# Revit family: LZSG8WSLK
name_source: partatom
category: Plumbing Fixtures
units: mm (PartAtom-declared; Revit-internal decimal feet)

## family parameters
Cut with Voids When Loaded = No
Host = Face
Part Type = Normal
Room Calculation Point = No
Round Connector Dimension = Use Diameter
Shared = No

## types (1)
- LZSG8WSLK
    ACTIVATION BY = ELECTRONIC BOTTLE FILLER SENOR WITH ELECTRONIC FRONT AND SIDE BUBBLER PUSHBAR
    APPROX. SHIPPING WEIGHT = 85 LBS
    BUBBLER STYLE = FLEXI-GUARD SAFTEY BUBBLER
    CHILLING OPTION = 8.0 GPH
    DIMENSIONS (LxWxH) = 18-3/8" x 19" x 39-1/16"
    Default Elevation = 2' - 3"
    FINISH = LIGHT GRAY GRANITE
    FULL LOAD AMPS = 7
    INSTALLATION LOCATION = INDOOR
    MOUNTING TYPE = WALL MOUNT
    NO OF STATIONS SERVED = 1
    POWER = 115V/60Hz
    RATED WATTS = 360
    SPECIAL FEATURES = HANDS FREE, VISUAL FILTER MONITOR, FILTERED, HIGH EFFICIENCY, GREEN TICKER, LAMINAR FLOW, ANTIMICROBIAL, REAL DRAIN

## geometry (parser evidence)
native form markers: Sweep x3
no freeform markers — native parametric forms only
